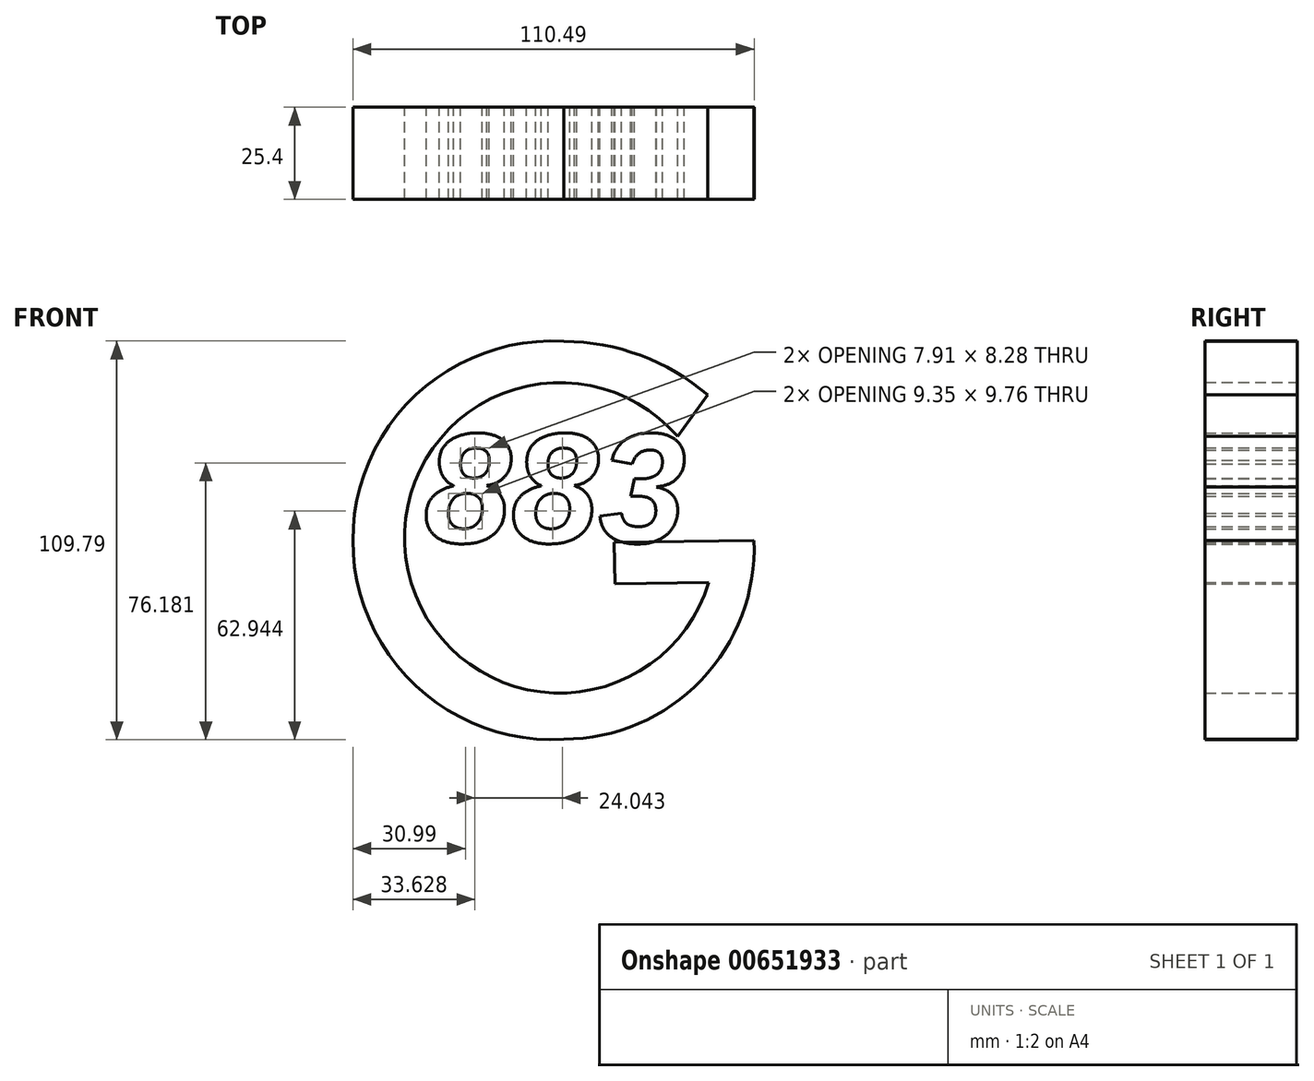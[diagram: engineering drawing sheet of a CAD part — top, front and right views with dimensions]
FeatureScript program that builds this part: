
annotation { "Feature Type Name" : "Feature", "Feature Type Description" : "" }
export const myFeature = defineFeature(function(context is Context, id is Id, definition is map)
    precondition{}
    {
        {
            var Q0;
            Q0=qCreatedBy(makeId("Front.planeOp"),FACE);
            var sketch = newSketch(context, id + "F0", { "sketchPlane" : qUnion([Q0])});
            skArc(sketch, "E0", {"start": v(0, 55.38) * mm, "mid": v(-58.12, 0.58) * mm, "end": v(0, -54.21) * mm});
            skArc(sketch, "E1", {"start": v(0, -54.21) * mm, "mid": v(37.8, -37.94) * mm, "end": v(52.32, 0.58) * mm});
            skArc(sketch, "E2", {"start": v(39.57, 40.65) * mm, "mid": v(21.1, 51.53) * mm, "end": v(0, 55.38) * mm});
            skLineSegment(sketch, "E3", {"start": v(52.32, 0.58) * mm, "end": v(13.87, 0) * mm});
            skLineSegment(sketch, "E4", {"start": v(13.87, 0) * mm, "end": v(14.04, -11.36) * mm});
            skLineSegment(sketch, "E5", {"start": v(14.04, -11.36) * mm, "end": v(39.87, -10.97) * mm});
            skArc(sketch, "E6", {"start": v(31.3, 29.19) * mm, "mid": v(-42.95, -7.64) * mm, "end": v(39.87, -10.97) * mm});
            skLineSegment(sketch, "E7", {"start": v(39.57, 40.65) * mm, "end": v(31.3, 29.19) * mm});
            skSolve(sketch);
        }
        {
            var Q0;
            Q0=qCreatedBy(makeId("Front.planeOp"),FACE);
            var sketch = newSketch(context, id + "F1", { "sketchPlane" : qUnion([Q0])});
            skText(sketch, "E8", { "text": "883", "fontName": "Arimo-BoldItalic.ttf"});
            const initialGuessF1  = {"E8": [-0.0385, 0, 1, 0, 0.03113]};
            skSetInitialGuess(sketch, initialGuessF1);
            skSolve(sketch);
        }
        {
            var Q0;
            Q0 = qSketchRegion(id + "F0", true);
            extrude(context, id + "F2", {"entities" : qUnion([Q0]), "depth" : 25.4 * mm, "offsetDistance" : 25.4 * mm});
        }
        {
            var Q0;
            Q0 = qSketchRegion(id + "F1", true);
            extrude(context, id + "F3", {"entities" : qUnion([Q0]), "depth" : 25.4 * mm, "offsetDistance" : 25.4 * mm});
        }
    });
